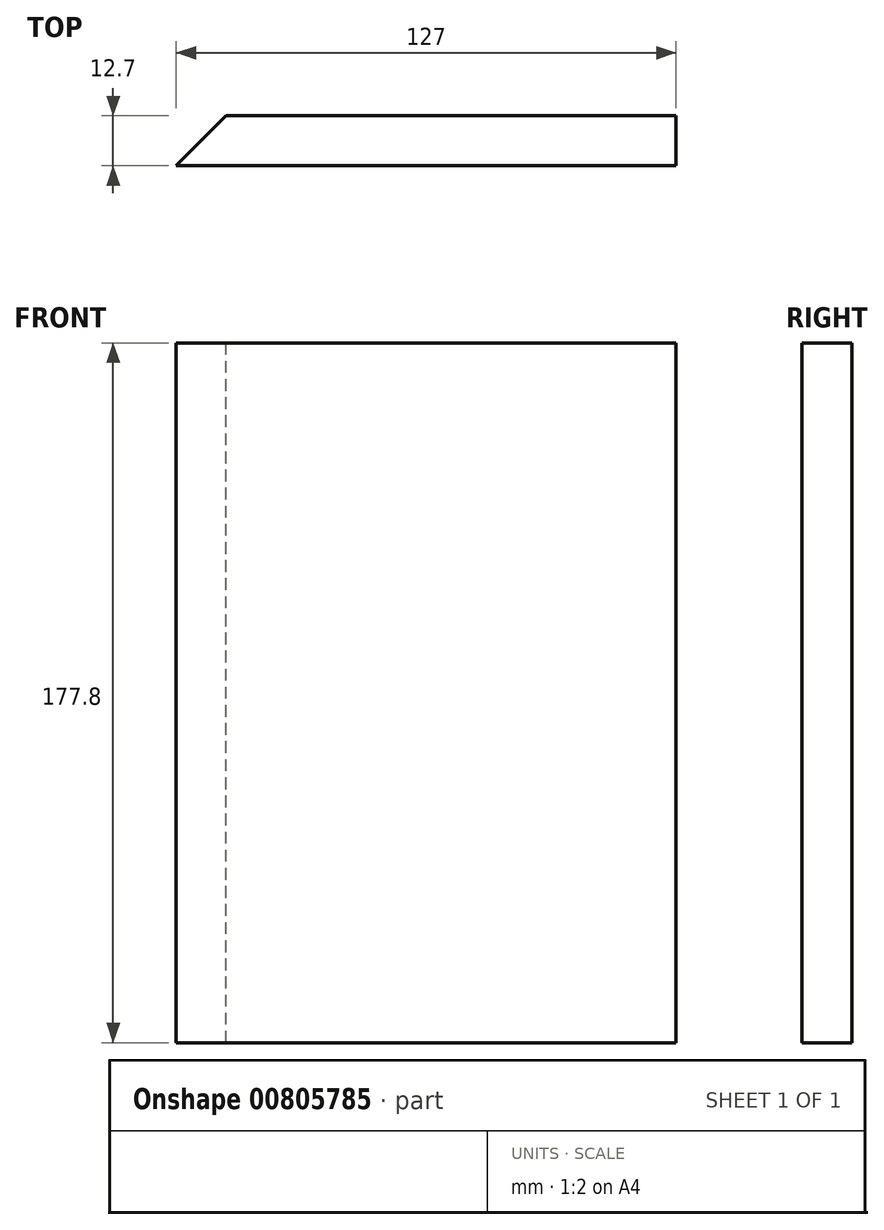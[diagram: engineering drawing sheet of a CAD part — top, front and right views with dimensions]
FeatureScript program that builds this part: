
annotation { "Feature Type Name" : "Feature", "Feature Type Description" : "" }
export const myFeature = defineFeature(function(context is Context, id is Id, definition is map)
    precondition{}
    {
        {
            var Q0;
            Q0=qCreatedBy(makeId("Front.planeOp"),FACE);
            var sketch = newSketch(context, id + "F0", { "sketchPlane" : qUnion([Q0])});
            skLineSegment(sketch, "E0.bottom", {"start": v(-63.5, 88.9) * mm, "end": v(63.5, 88.9) * mm});
            skLineSegment(sketch, "E0.top", {"start": v(-63.5, -88.9) * mm, "end": v(63.5, -88.9) * mm});
            skLineSegment(sketch, "E0.left", {"start": v(-63.5, 88.9) * mm, "end": v(-63.5, -88.9) * mm});
            skLineSegment(sketch, "E0.right", {"start": v(63.5, 88.9) * mm, "end": v(63.5, -88.9) * mm});
            skLineSegment(sketch, "E1", {"start": v(0, 88.9) * mm, "end": v(0, -88.9) * mm, "construction": true});
            skLineSegment(sketch, "E2", {"start": v(-63.5, 0) * mm, "end": v(63.5, 0) * mm, "construction": true});
            skSolve(sketch);
        }
        {
            var Q0;
            Q0=qSketchRegion(id+"F0",true);
            extrude(context, id + "F1", {"entities" : qUnion([Q0]), "depth" : 12.7 * mm, "offsetDistance" : 25.4 * mm});
        }
        {
            var Q0;
            Q0=makeQuery(id+"F1.opExtrude","SWEPT_FACE",FACE,{"disambiguationData":[OSD([sQuery(id+"F0.wireOp",EDGE,"E0.bottom")])]});
            var sketch = newSketch(context, id + "F2", { "sketchPlane" : qUnion([Q0])});
            skLineSegment(sketch, "E3", {"start": v(-50.8, 0) * mm, "end": v(-63.5, -12.7) * mm});
            skLineSegment(sketch, "E4", {"start": v(-63.5, -12.7) * mm, "end": v(-63.5, 0) * mm});
            skLineSegment(sketch, "E5", {"start": v(-50.8, 0) * mm, "end": v(-63.5, 0) * mm});
            skSolve(sketch);
        }
        {
            var Q0;
            Q0 = qSketchRegion(id + "F2", true);
            extrude(context, id + "F3", {"entities" : qUnion([Q0]), "operationType" : NewBodyOperationType.REMOVE, "endBound" : BoundingType.THROUGH_ALL, "oppositeDirection" : true, "depth" : 25.4 * mm, "offsetDistance" : 25.4 * mm});
        }
    });
